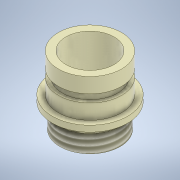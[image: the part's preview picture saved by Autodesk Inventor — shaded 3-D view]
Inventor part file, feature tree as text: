
AUTODESK INVENTOR PART (.ipt)
format: ipt  version: 2020 (Build 240168000, 168)  size: 158,208 bytes
history: native  units: mm
features: revolve x1, thread x1
ambient origin geometry x8: Origin, YZ Plane, XZ Plane, XY Plane, X Axis, Y Axis, Z Axis, Center Point
bodies: Body1 (feature_tree)
feature tree (2):
  revolve  "Revolution2"  [1 undecoded]
  thread  "Thread3"  [1 undecoded]
note: 2 required parameter values undecoded (feature->parameter linkage not recoverable at this tier; creation-order binding heuristic only, values carry confidence <= 0.55)